# Revit family: Haworth_Cabana_LoungeIsland
name_source: partatom
category: Furniture
revit_build: Autodesk Revit 2018 (Build: 20170223_1515(x64)
units: mm (PartAtom-declared; Revit-internal decimal feet)

## family parameters
Always vertical = Yes
Cut with Voids When Loaded = No
OmniClass Number = 23.40.70.14.64.21
OmniClass Title = Systems Furniture
Room Calculation Point = No
Shared = No
Work Plane-Based = No

## types (4) — shared parameters
Actual Depth = 55"
Actual Height = 30 3/8"
Actual Width = 72"
Assembly Code = E2020200
Leg Offset = 2 1/2"
Manufacturer = Haworth
Model = Haworth Cabana Island
Revision Number = 1
Seat Height = 18 1/16"
Size = Verify Final Dim. w/ Haworth
Table Offset = 10 5/8"
URL = http://www.haworth.com
URL - Product = http://www.haworth.com
Warranty = http://www.haworth.com

## per-type parameters (varying)
| type | Back Width | Description | Full Back | Half Back | With Top |
| Full Back - With Integrated Table | 72" | Haworth Cabana Island - Full Back - With Integrated Table | Yes | No | Yes |
| Full Back - Without Integrated Table | 72" | Haworth Cabana Island - Full Back - Without Integrated Table | Yes | No | No |
| Half Back - With Integrated Table | 43 3/64" | Haworth Cabana Island - Half Back - With Integrated Table | No | Yes | Yes |
| Half Back - Without Integrated Table | 43 3/64" | Haworth Cabana Island - Half Back - Without Integrated Table | No | Yes | No |

## geometry (parser evidence)
native form markers: Extrusion x4, Sweep x11
no freeform markers — native parametric forms only
